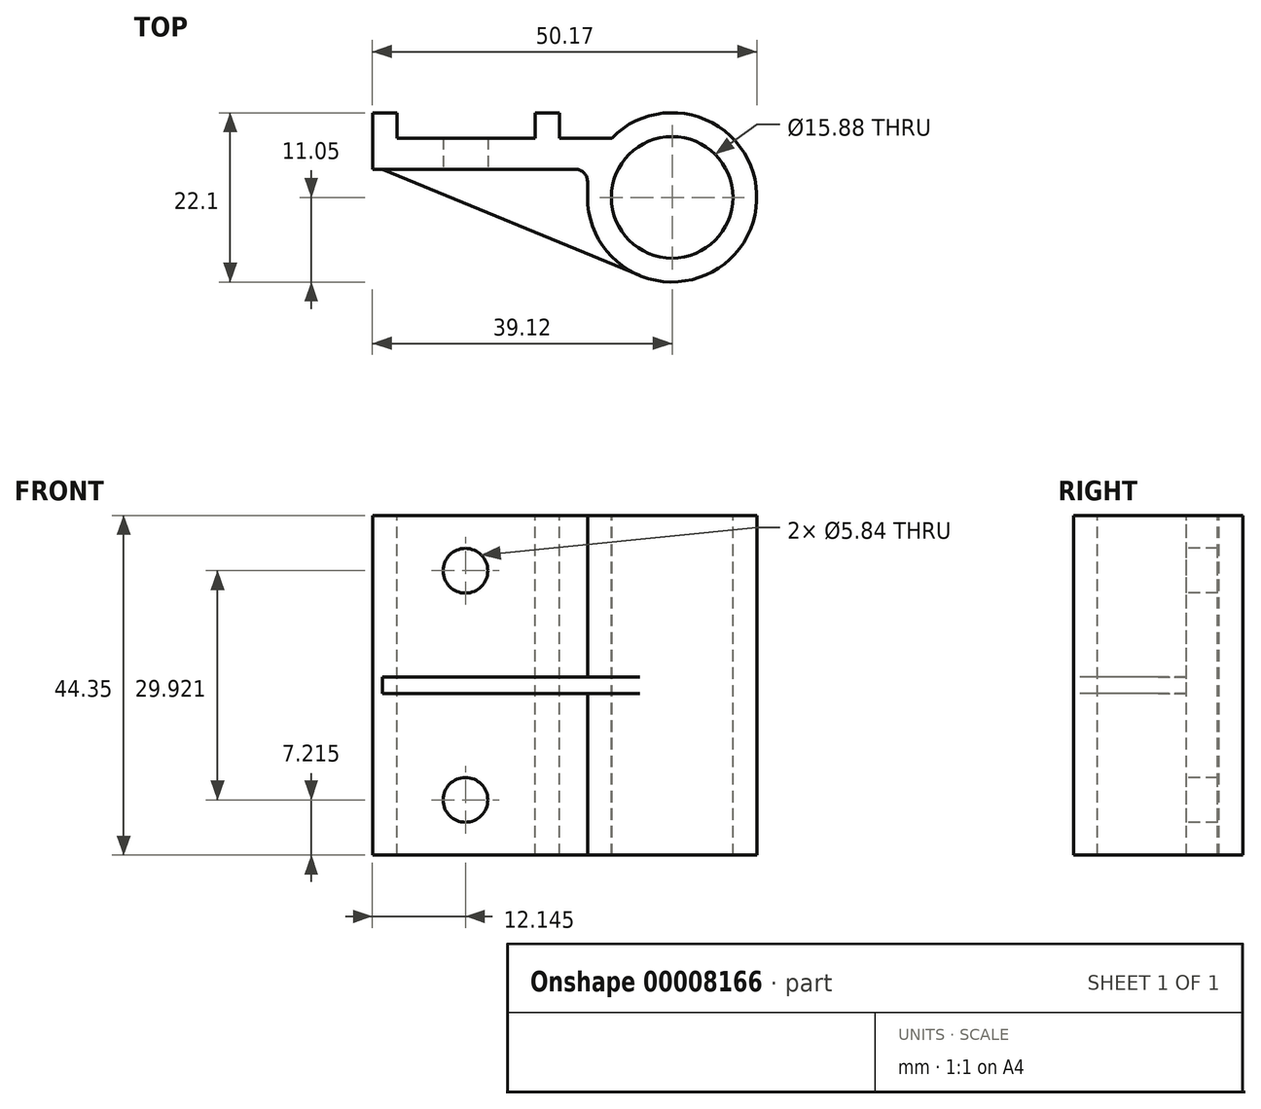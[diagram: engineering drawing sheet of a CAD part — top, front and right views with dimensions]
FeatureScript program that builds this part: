
annotation { "Feature Type Name" : "Feature", "Feature Type Description" : "" }
export const myFeature = defineFeature(function(context is Context, id is Id, definition is map)
    precondition{}
    {
        {
            var Q0;
            Q0=qCreatedBy(makeId("Top.planeOp"),FACE);
            var sketch = newSketch(context, id + "F0", { "sketchPlane" : qUnion([Q0])});
            skArc(sketch, "E0", {"start": v(-11.05, 0) * mm, "mid": v(10.23, -4.19) * mm, "end": v(-7.88, 7.75) * mm});
            skCircle(sketch, "E1", {"center": v(0, 0) * mm, "radius": 5.02 * mm});
            skLineSegment(sketch, "E2", {"start": v(-14.73, 11.05) * mm, "end": v(-17.9, 11.05) * mm});
            skLineSegment(sketch, "E3", {"start": v(-39.12, 11.05) * mm, "end": v(-39.12, 3.68) * mm});
            skLineSegment(sketch, "E4", {"start": v(-39.12, 3.68) * mm, "end": v(-12.64, 3.68) * mm});
            skLineSegment(sketch, "E5", {"start": v(-35.94, 11.05) * mm, "end": v(-35.94, 7.75) * mm});
            skLineSegment(sketch, "E6", {"start": v(-35.94, 7.75) * mm, "end": v(-17.9, 7.75) * mm});
            skLineSegment(sketch, "E7", {"start": v(-17.9, 7.75) * mm, "end": v(-17.9, 11.05) * mm});
            skLineSegment(sketch, "E8", {"start": v(-14.73, 11.05) * mm, "end": v(-14.73, 7.75) * mm});
            skLineSegment(sketch, "E9", {"start": v(-14.73, 7.75) * mm, "end": v(-7.88, 7.75) * mm});
            skLineSegment(sketch, "E10.trimOffspring", {"start": v(-35.94, 11.05) * mm, "end": v(-39.12, 11.05) * mm});
            skLineSegment(sketch, "E11", {"start": v(-11.05, 2.1) * mm, "end": v(-11.05, 0) * mm});
            skPoint(sketch, "E12.visualSharp", {"position": v(-11.05, 3.68) * mm});
            skArc(sketch, "E12.filletArc", {"start": v(-11.05, 2.1) * mm, "mid": v(-11.51, 3.22) * mm, "end": v(-12.64, 3.68) * mm});
            skSolve(sketch);
        }
        {
            var Q0;
            Q0 = qSketchRegion(id + "F0", true);
            extrude(context, id + "F1", {"entities" : qUnion([Q0]), "oppositeDirection" : true, "depth" : 44.35 * mm});
        }
        {
            var Q0;
            Q0=qCreatedBy(makeId("Top.planeOp"),FACE);
            cPlane(context, id + "F2", {"entities" : qUnion([Q0]), "cplaneType" : CPlaneType.OFFSET, "offset" : 22.17 * mm, "oppositeDirection" : true, "width" : 152.4 * mm, "height" : 152.4 * mm});
        }
        {
            var Q0;
            Q0=qCreatedBy(id+"F2.planeOp",FACE);
            var sketch = newSketch(context, id + "F3", { "sketchPlane" : qUnion([Q0])});
            skLineSegment(sketch, "E13", {"start": v(-39.12, 4.2) * mm, "end": v(-4.22, -10.21) * mm});
            skLineSegment(sketch, "E14", {"start": v(0, -11.05) * mm, "end": v(0, -5.02) * mm});
            skLineSegment(sketch, "E15", {"start": v(-2.73, 4.2) * mm, "end": v(-39.12, 4.2) * mm});
            skLineSegment(sketch, "E16", {"start": v(-37.85, 1.72) * mm, "end": v(-37.85, 9.66) * mm, "construction": true});
            skPoint(sketch, "E17", {"position": v(-37.85, 3.68) * mm});
            skArc(sketch, "E18", {"start": v(-2.73, 4.2) * mm, "mid": v(-4.81, -1.42) * mm, "end": v(0, -5.02) * mm});
            skPoint(sketch, "E19.orphan", {"position": v(0, 4.2) * mm});
            skArc(sketch, "E20", {"start": v(-4.22, -10.21) * mm, "mid": v(-2.15, -10.84) * mm, "end": v(0, -11.05) * mm});
            skPoint(sketch, "E21.orphan", {"position": v(0, -11.96) * mm});
            skSolve(sketch);
        }
        {
            var Q0;
            Q0 = qSketchRegion(id + "F3", true);
            extrude(context, id + "F4", {"entities" : qUnion([Q0]), "operationType" : NewBodyOperationType.ADD, "endBound" : BoundingType.SYMMETRIC, "depth" : 2.18 * mm});
        }
        {
            var Q0;
            Q0=makeQuery(id+"F1.opExtrude","SWEPT_FACE",FACE,{"disambiguationData":[OSD([sQuery(id+"F0.wireOp",EDGE,"E4")])]});
            var sketch = newSketch(context, id + "F5", { "sketchPlane" : qUnion([Q0])});
            skCircle(sketch, "E22", {"center": v(-26.97, -7.21) * mm, "radius": 2.92 * mm});
            skCircle(sketch, "E23", {"center": v(-26.97, -37.13) * mm, "radius": 2.92 * mm});
            skSolve(sketch);
        }
        {
            var Q0;
            Q0 = qSketchRegion(id + "F5", true);
            var Q1;
            Q1=makeQuery(id+"F1.opExtrude","SWEPT_FACE",FACE,{"disambiguationData":[OSD([sQuery(id+"F0.wireOp",EDGE,"E6")])]});
            extrude(context, id + "F6", {"entities" : qUnion([Q0]), "operationType" : NewBodyOperationType.REMOVE, "endBound" : BoundingType.UP_TO_SURFACE, "oppositeDirection" : true, "endBoundEntityFace" : qUnion([Q1]), "depth" : 25.4 * mm});
        }
        {
            var Q0;
            Q0=makeQuery(id+"F1.opExtrude","CAP_FACE",FACE,{"disambiguationData":[OSD([sQuery(id+"F0.wireOp",EDGE,"E0"),sQuery(id+"F0.wireOp",EDGE,"E1"),sQuery(id+"F0.wireOp",EDGE,"E2"),sQuery(id+"F0.wireOp",EDGE,"E3"),sQuery(id+"F0.wireOp",EDGE,"E4"),sQuery(id+"F0.wireOp",EDGE,"E5"),sQuery(id+"F0.wireOp",EDGE,"E6"),sQuery(id+"F0.wireOp",EDGE,"E7"),sQuery(id+"F0.wireOp",EDGE,"E8"),sQuery(id+"F0.wireOp",EDGE,"E9"),sQuery(id+"F0.wireOp",EDGE,"E10.trimOffspring"),sQuery(id+"F0.wireOp",EDGE,"E11"),sQuery(id+"F0.wireOp",EDGE,"E12.filletArc")])],"isStart":true});
            var sketch = newSketch(context, id + "F7", { "sketchPlane" : qUnion([Q0])});
            skCircle(sketch, "E24", {"center": v(0, 0) * mm, "radius": 7.94 * mm});
            skCircle(sketch, "E25", {"center": v(0, 0) * mm, "radius": 5.02 * mm});
            skSolve(sketch);
        }
        {
            var Q0;
            Q0 = qSketchRegion(id + "F7", true);
            var Q1;
            Q1=makeQuery(id+"F1.opExtrude","CAP_FACE",FACE,{"disambiguationData":[OSD([sQuery(id+"F0.wireOp",EDGE,"E0"),sQuery(id+"F0.wireOp",EDGE,"E1"),sQuery(id+"F0.wireOp",EDGE,"E2"),sQuery(id+"F0.wireOp",EDGE,"E3"),sQuery(id+"F0.wireOp",EDGE,"E4"),sQuery(id+"F0.wireOp",EDGE,"E5"),sQuery(id+"F0.wireOp",EDGE,"E6"),sQuery(id+"F0.wireOp",EDGE,"E7"),sQuery(id+"F0.wireOp",EDGE,"E8"),sQuery(id+"F0.wireOp",EDGE,"E9"),sQuery(id+"F0.wireOp",EDGE,"E10.trimOffspring"),sQuery(id+"F0.wireOp",EDGE,"E11"),sQuery(id+"F0.wireOp",EDGE,"E12.filletArc")])],"isStart":false});
            extrude(context, id + "F8", {"entities" : qUnion([Q0]), "operationType" : NewBodyOperationType.REMOVE, "endBound" : BoundingType.UP_TO_SURFACE, "oppositeDirection" : true, "endBoundEntityFace" : qUnion([Q1]), "depth" : 25.4 * mm});
        }
    });
